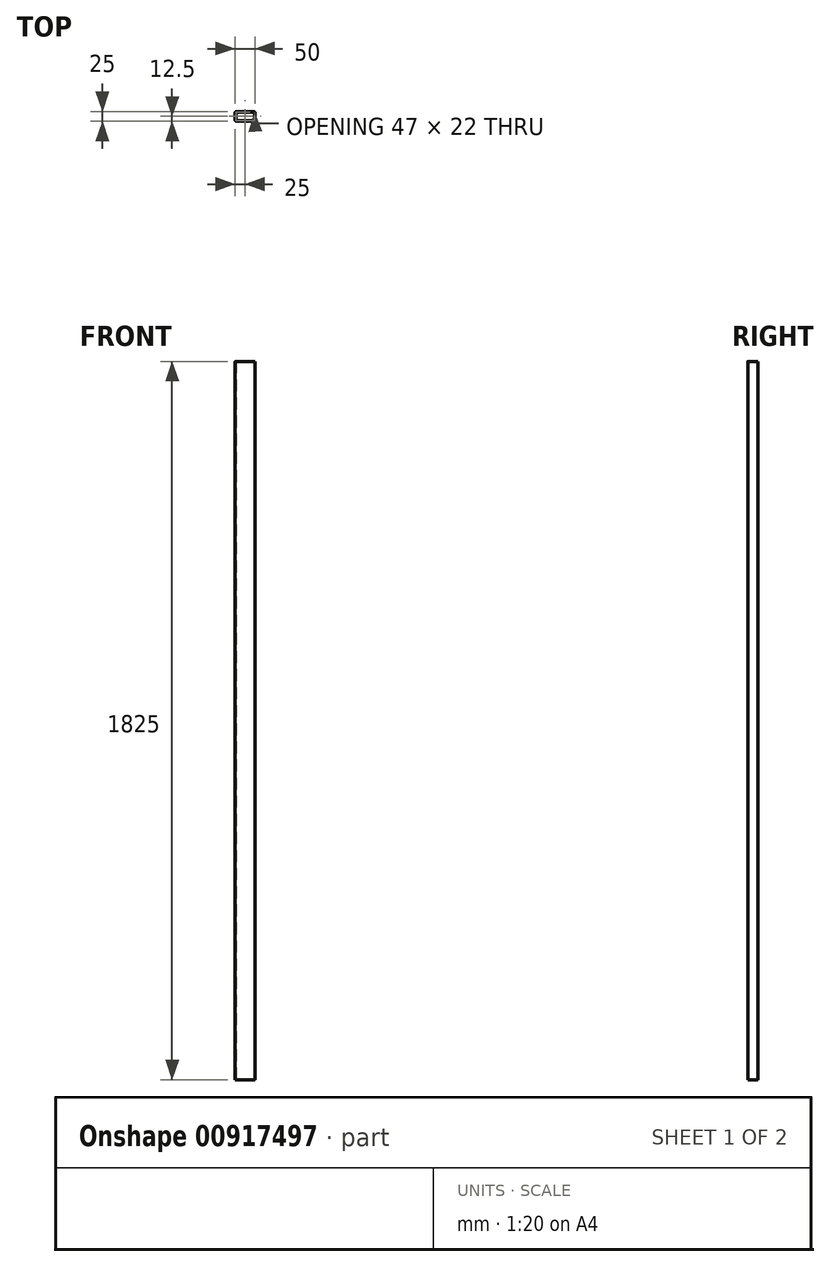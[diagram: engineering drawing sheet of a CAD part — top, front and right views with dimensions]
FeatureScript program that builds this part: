
annotation { "Feature Type Name" : "Feature", "Feature Type Description" : "" }
export const myFeature = defineFeature(function(context is Context, id is Id, definition is map)
    precondition{}
    {
        {
            var Q0;
            Q0=qCreatedBy(makeId("Top.planeOp"),FACE);
            var sketch = newSketch(context, id + "F0", { "sketchPlane" : qUnion([Q0])});
            skLineSegment(sketch, "E0.bottom", {"start": v(22.5, 12.5) * mm, "end": v(-22.5, 12.5) * mm});
            skLineSegment(sketch, "E0.top", {"start": v(22.5, -12.5) * mm, "end": v(-22.5, -12.5) * mm});
            skLineSegment(sketch, "E0.left", {"start": v(25, 10) * mm, "end": v(25, -10) * mm});
            skLineSegment(sketch, "E0.right", {"start": v(-25, 10) * mm, "end": v(-25, -10) * mm});
            skPoint(sketch, "E0.middle", {"position": v(0, 0) * mm});
            skPoint(sketch, "E1.visualSharp", {"position": v(-25, 12.5) * mm});
            skArc(sketch, "E1.filletArc", {"start": v(-22.5, 12.5) * mm, "mid": v(-24.27, 11.77) * mm, "end": v(-25, 10) * mm});
            skPoint(sketch, "E2.visualSharp", {"position": v(25, 12.5) * mm});
            skArc(sketch, "E2.filletArc", {"start": v(25, 10) * mm, "mid": v(24.27, 11.77) * mm, "end": v(22.5, 12.5) * mm});
            skPoint(sketch, "E3.visualSharp", {"position": v(25, -12.5) * mm});
            skArc(sketch, "E3.filletArc", {"start": v(22.5, -12.5) * mm, "mid": v(24.27, -11.77) * mm, "end": v(25, -10) * mm});
            skPoint(sketch, "E4.visualSharp", {"position": v(-25, -12.5) * mm});
            skArc(sketch, "E4.filletArc", {"start": v(-25, -10) * mm, "mid": v(-24.27, -11.77) * mm, "end": v(-22.5, -12.5) * mm});
            skLineSegment(sketch, "E5.0", {"start": v(22.5, -11) * mm, "end": v(-22.5, -11) * mm});
            skLineSegment(sketch, "E5.1", {"start": v(23.5, 11) * mm, "end": v(23.5, -10) * mm});
            skLineSegment(sketch, "E5.2", {"start": v(23.5, 11) * mm, "end": v(-22.5, 11) * mm});
            skLineSegment(sketch, "E5.3", {"start": v(-23.5, 10) * mm, "end": v(-23.5, -10) * mm});
            skPoint(sketch, "E6.visualSharp", {"position": v(-23.5, -11) * mm});
            skArc(sketch, "E6.filletArc", {"start": v(-23.5, -10) * mm, "mid": v(-23.2, -10.7) * mm, "end": v(-22.5, -11) * mm});
            skPoint(sketch, "E7.visualSharp", {"position": v(-23.5, 11) * mm});
            skArc(sketch, "E7.filletArc", {"start": v(-22.5, 11) * mm, "mid": v(-23.2, 10.7) * mm, "end": v(-23.5, 10) * mm});
            skPoint(sketch, "E8.visualSharp", {"position": v(23.5, -11) * mm});
            skArc(sketch, "E8.filletArc", {"start": v(22.5, -11) * mm, "mid": v(23.2, -10.7) * mm, "end": v(23.5, -10) * mm});
            skSolve(sketch);
        }
        {
            var Q0;
            Q0=qSketchRegion(id+"F0",true);
            extrude(context, id + "F1", {"entities" : qUnion([Q0]), "depth" : (2000 - 25 - 150) * mm, "offsetDistance" : 25 * mm});
        }
    });
